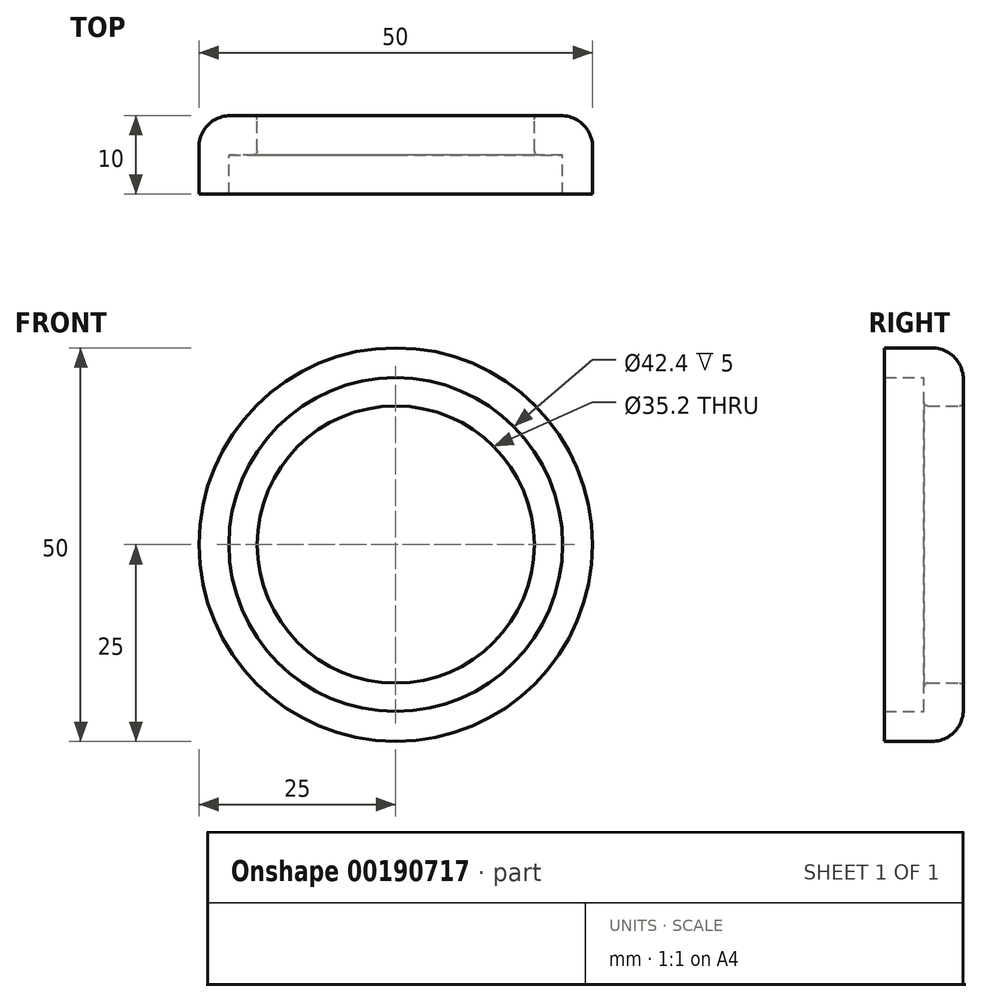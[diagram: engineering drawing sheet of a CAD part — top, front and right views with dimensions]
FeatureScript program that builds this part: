
annotation { "Feature Type Name" : "Feature", "Feature Type Description" : "" }
export const myFeature = defineFeature(function(context is Context, id is Id, definition is map)
    precondition{}
    {
        {
            var Q0;
            Q0=qCreatedBy(makeId("Front.planeOp"),FACE);
            var sketch = newSketch(context, id + "F0", { "sketchPlane" : qUnion([Q0])});
            skCircle(sketch, "E0", {"center": v(0, 0) * mm, "radius": 21.2 * mm});
            skCircle(sketch, "E1", {"center": v(0, 0) * mm, "radius": 25 * mm});
            skLineSegment(sketch, "E2", {"start": v(21.2, 0) * mm, "end": v(25, 0) * mm, "construction": true});
            skSolve(sketch);
        }
        {
            var Q0;
            Q0 = qSketchRegion(id + "F0", true);
            extrude(context, id + "F1", {"entities" : qUnion([Q0]), "depth" : 5 * mm, "offsetDistance" : 25 * mm});
        }
        {
            var Q0;
            Q0=qCreatedBy(makeId("Top.planeOp"),FACE);
            var sketch = newSketch(context, id + "F2", { "sketchPlane" : qUnion([Q0])});
            skLineSegment(sketch, "E3", {"start": v(17.6, 0.5) * mm, "end": v(17.6, 4.5) * mm});
            skLineSegment(sketch, "E4", {"start": v(18.1, 5) * mm, "end": v(21, 5) * mm});
            skLineSegment(sketch, "E5", {"start": v(25, 1) * mm, "end": v(25, 0) * mm});
            skLineSegment(sketch, "E6", {"start": v(25, 0) * mm, "end": v(18.1, 0) * mm});
            skPoint(sketch, "E7.visualSharp", {"position": v(17.6, 5) * mm});
            skArc(sketch, "E7.filletArc", {"start": v(18.1, 5) * mm, "mid": v(17.75, 4.85) * mm, "end": v(17.6, 4.5) * mm});
            skPoint(sketch, "E8.visualSharp", {"position": v(25, 5) * mm});
            skArc(sketch, "E8.filletArc", {"start": v(25, 1) * mm, "mid": v(23.83, 3.83) * mm, "end": v(21, 5) * mm});
            skLineSegment(sketch, "E9.0.0", {"start": v(25, 0) * mm, "end": v(-25, 0) * mm});
            skPoint(sketch, "E10.0", {"position": v(17.6, 0) * mm});
            skPoint(sketch, "E11.0", {"position": v(21.2, 0) * mm});
            skArc(sketch, "E12.filletArc", {"start": v(17.6, 0.5) * mm, "mid": v(17.75, 0.15) * mm, "end": v(18.1, 0) * mm});
            skSolve(sketch);
        }
        {
            var Q0;
            Q0 = qSketchRegion(id + "F2", true);
            var Q1;
            Q1=sQuery(id+"F0.wireOp",EDGE,"E0");
            revolve(context, id + "F3", {"operationType" : NewBodyOperationType.ADD, "entities" : qUnion([Q0]), "axis" : qUnion([Q1]), "revolveType" : RevolveType.FULL});
        }
    });
